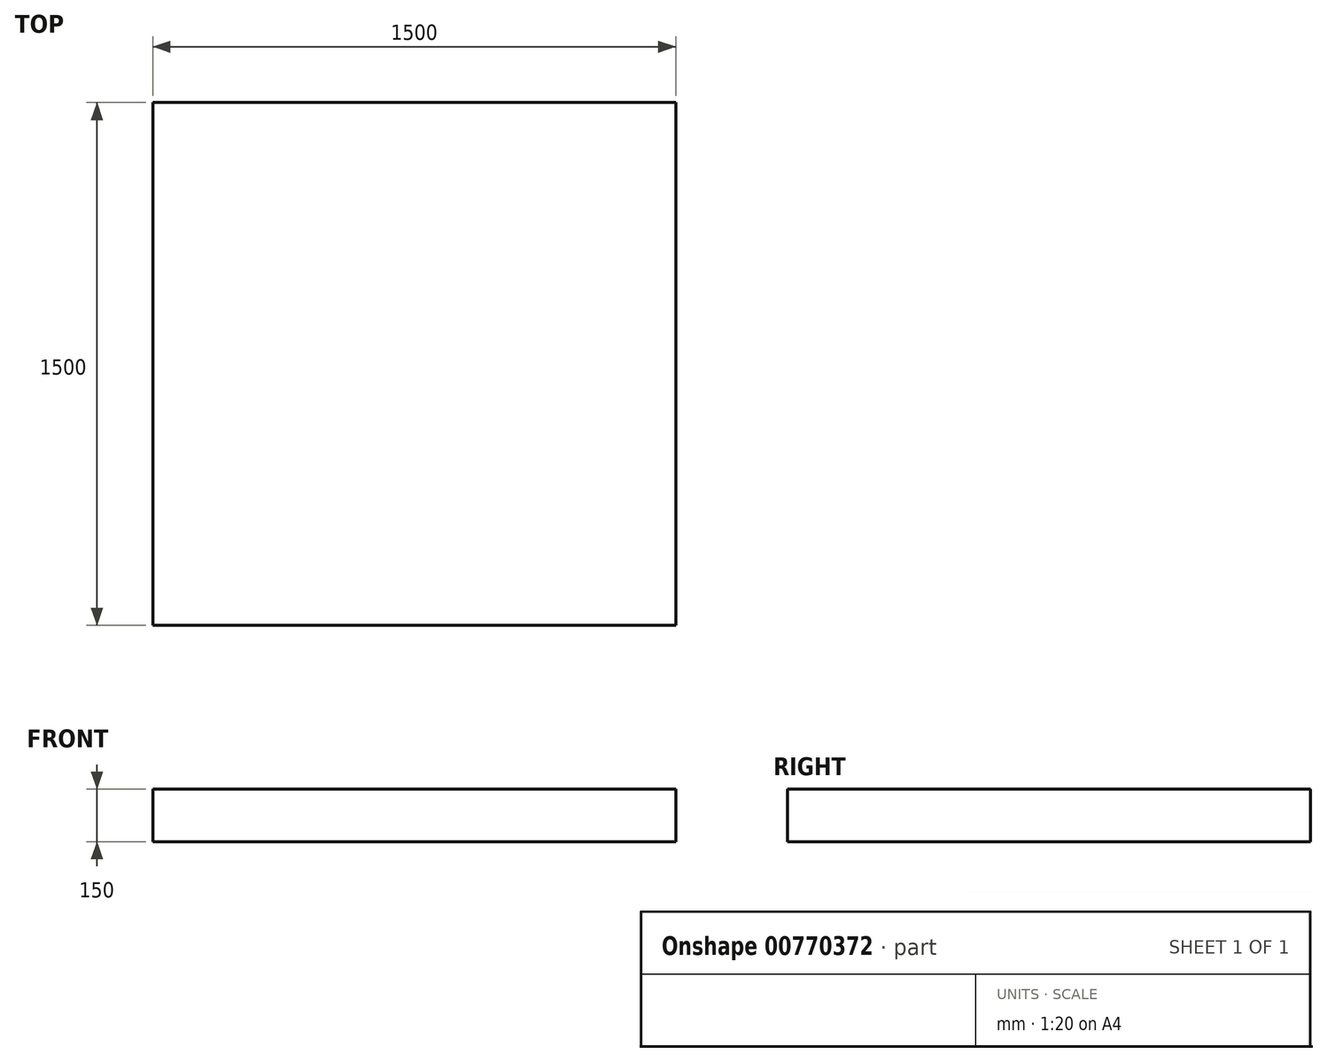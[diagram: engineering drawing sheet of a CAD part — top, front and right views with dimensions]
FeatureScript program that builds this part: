
annotation { "Feature Type Name" : "Feature", "Feature Type Description" : "" }
export const myFeature = defineFeature(function(context is Context, id is Id, definition is map)
    precondition{}
    {
        {
            var Q0;
            Q0=qCreatedBy(makeId("Top.planeOp"),FACE);
            var sketch = newSketch(context, id + "F0", { "sketchPlane" : qUnion([Q0])});
            skLineSegment(sketch, "E0.bottom", {"start": v(0, 0) * mm, "end": v(1500, 0) * mm});
            skLineSegment(sketch, "E0.top", {"start": v(0, 1500) * mm, "end": v(1500, 1500) * mm});
            skLineSegment(sketch, "E0.left", {"start": v(0, 0) * mm, "end": v(0, 1500) * mm});
            skLineSegment(sketch, "E0.right", {"start": v(1500, 0) * mm, "end": v(1500, 1500) * mm});
            skSolve(sketch);
        }
        {
            var Q0;
            Q0=makeQuery(id+"F0.imprint","IMPRINT",FACE,{"disambiguationData":[TD([[makeQuery(id+"F0.imprint","IMPRINT",EDGE,{"derivedFrom":sQuery(id+"F0.wireOp",EDGE,"E0.bottom")}),1.0]])]});
            extrude(context, id + "F1", {"entities" : qUnion([Q0]), "depth" : 150 * mm, "offsetDistance" : 25 * mm});
        }
    });
